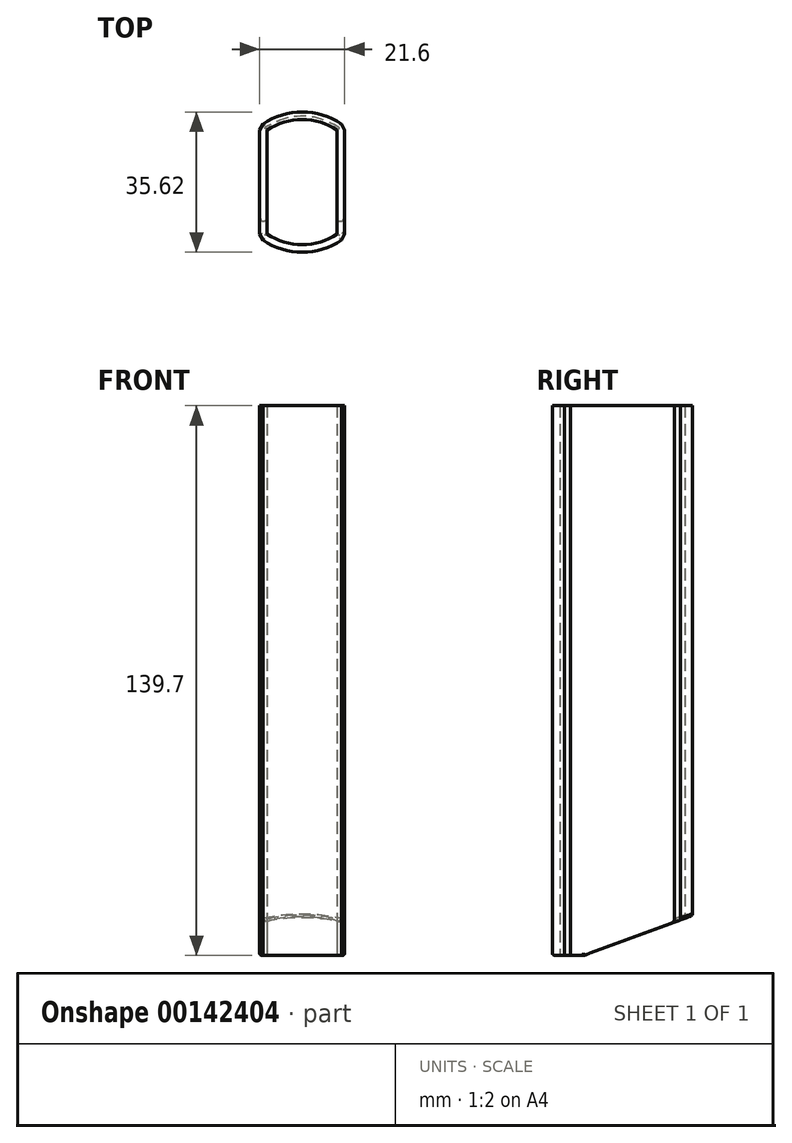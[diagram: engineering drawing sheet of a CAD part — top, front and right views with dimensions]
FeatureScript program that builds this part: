
annotation { "Feature Type Name" : "Feature", "Feature Type Description" : "" }
export const myFeature = defineFeature(function(context is Context, id is Id, definition is map)
    precondition{}
    {
        {
            var Q0;
            Q0=qCreatedBy(makeId("Top.planeOp"),FACE);
            var sketch = newSketch(context, id + "F0", { "sketchPlane" : qUnion([Q0])});
            skLineSegment(sketch, "E0.bottom", {"start": v(-8.9, 13.15) * mm, "end": v(8.9, 13.15) * mm, "construction": true});
            skLineSegment(sketch, "E0.top", {"start": v(-8.9, -13.15) * mm, "end": v(8.9, -13.15) * mm, "construction": true});
            skLineSegment(sketch, "E0.left", {"start": v(-8.9, 13.15) * mm, "end": v(-8.9, -13.15) * mm});
            skLineSegment(sketch, "E0.right", {"start": v(8.9, 13.15) * mm, "end": v(8.9, -13.15) * mm});
            skPoint(sketch, "E0.middle", {"position": v(0, 0) * mm});
            skArc(sketch, "E1", {"start": v(8.9, 13.15) * mm, "mid": v(0, 15.9) * mm, "end": v(-8.9, 13.15) * mm});
            skArc(sketch, "E2", {"start": v(-8.9, -13.15) * mm, "mid": v(0, -15.9) * mm, "end": v(8.89, -13.15) * mm});
            skLineSegment(sketch, "E3.0", {"start": v(-10.8, 13.15) * mm, "end": v(-10.8, -13.15) * mm});
            skArc(sketch, "E4.0", {"start": v(9.97, 14.72) * mm, "mid": v(0, 17.8) * mm, "end": v(-9.97, 14.72) * mm});
            skLineSegment(sketch, "E5.0", {"start": v(10.8, 13.15) * mm, "end": v(10.8, -13.15) * mm});
            skArc(sketch, "E6.0", {"start": v(-9.97, -14.72) * mm, "mid": v(0, -17.8) * mm, "end": v(9.97, -14.72) * mm});
            skLineSegment(sketch, "E7", {"start": v(-10.8, 13.15) * mm, "end": v(-9.97, 14.72) * mm});
            skLineSegment(sketch, "E8", {"start": v(9.97, 14.72) * mm, "end": v(10.8, 13.15) * mm});
            skLineSegment(sketch, "E9", {"start": v(-9.97, -14.72) * mm, "end": v(-10.8, -13.15) * mm});
            skLineSegment(sketch, "E10", {"start": v(9.97, -14.72) * mm, "end": v(10.8, -13.15) * mm});
            skSolve(sketch);
        }
        {
            var Q0;
            Q0=makeQuery(id+"F0.imprint","IMPRINT",FACE,{"disambiguationData":[TD([[makeQuery(id+"F0.imprint","IMPRINT",EDGE,{"derivedFrom":sQuery(id+"F0.wireOp",EDGE,"E0.left")}),-1.0]])]});
            extrude(context, id + "F1", {"entities" : qUnion([Q0]), "depth" : 139.7 * mm});
        }
        {
            var Q0;
            Q0=qCreatedBy(makeId("Right.planeOp"),FACE);
            var sketch = newSketch(context, id + "F2", { "sketchPlane" : qUnion([Q0])});
            skLineSegment(sketch, "E11", {"start": v(-9.84, 0) * mm, "end": v(0, 0) * mm});
            skLineSegment(sketch, "E12", {"start": v(0, 0) * mm, "end": v(24.65, 0) * mm});
            skLineSegment(sketch, "E13", {"start": v(24.65, 0) * mm, "end": v(24.65, 12.7) * mm});
            skLineSegment(sketch, "E14", {"start": v(24.65, 12.7) * mm, "end": v(-9.84, 0) * mm});
            skSolve(sketch);
        }
        {
            var Q0;
            Q0 = qSketchRegion(id + "F2", true);
            extrude(context, id + "F3", {"entities" : qUnion([Q0]), "operationType" : NewBodyOperationType.REMOVE, "endBound" : BoundingType.SYMMETRIC, "oppositeDirection" : true, "depth" : 21.59 * mm});
        }
        {
            var Q0;
            Q0=makeQuery(id+"F3.boolean.opBoolean","COPY",EDGE,{"derivedFrom":makeQuery(id+"F3.opExtrude","CAP_EDGE",EDGE,{"disambiguationData":[OSD([sQuery(id+"F2.wireOp",EDGE,"E14")])],"isStart":false})});
            var Q1;
            Q1=makeQuery(id+"F3.boolean.opBoolean","INTERSECT",EDGE,{"derivedFrom":[makeQuery(id+"F1.opExtrude","SWEPT_FACE",FACE,{"disambiguationData":[OSD([sQuery(id+"F0.wireOp",EDGE,"E4.0")])]}),makeQuery(id+"F3.opExtrude","SWEPT_FACE",FACE,{"disambiguationData":[OSD([sQuery(id+"F2.wireOp",EDGE,"E14")])]})]});
            var Q2;
            Q2=makeQuery(id+"F3.boolean.opBoolean","INTERSECT",EDGE,{"derivedFrom":[makeQuery(id+"F1.opExtrude","SWEPT_FACE",FACE,{"disambiguationData":[OSD([sQuery(id+"F0.wireOp",EDGE,"E1")])]}),makeQuery(id+"F3.opExtrude","SWEPT_FACE",FACE,{"disambiguationData":[OSD([sQuery(id+"F2.wireOp",EDGE,"E14")])]})]});
            var Q3;
            Q3=makeQuery(id+"F3.boolean.opBoolean","INTERSECT",EDGE,{"derivedFrom":[makeQuery(id+"F1.opExtrude","SWEPT_FACE",FACE,{"disambiguationData":[OSD([sQuery(id+"F0.wireOp",EDGE,"E0.right")])]}),makeQuery(id+"F3.opExtrude","SWEPT_FACE",FACE,{"disambiguationData":[OSD([sQuery(id+"F2.wireOp",EDGE,"E14")])]})]});
            var Q4;
            Q4=makeQuery(id+"F3.boolean.opBoolean","COPY",EDGE,{"derivedFrom":makeQuery(id+"F3.opExtrude","CAP_EDGE",EDGE,{"disambiguationData":[OSD([sQuery(id+"F2.wireOp",EDGE,"E14")])],"isStart":true})});
            var Q5;
            Q5=makeQuery(id+"F3.boolean.opBoolean","INTERSECT",EDGE,{"derivedFrom":[makeQuery(id+"F1.opExtrude","SWEPT_FACE",FACE,{"disambiguationData":[OSD([sQuery(id+"F0.wireOp",EDGE,"E8")])]}),makeQuery(id+"F3.opExtrude","SWEPT_FACE",FACE,{"disambiguationData":[OSD([sQuery(id+"F2.wireOp",EDGE,"E14")])]})]});
            var Q6;
            Q6=makeQuery(id+"F3.boolean.opBoolean","INTERSECT",EDGE,{"derivedFrom":[makeQuery(id+"F1.opExtrude","SWEPT_FACE",FACE,{"disambiguationData":[OSD([sQuery(id+"F0.wireOp",EDGE,"E7")])]}),makeQuery(id+"F3.opExtrude","SWEPT_FACE",FACE,{"disambiguationData":[OSD([sQuery(id+"F2.wireOp",EDGE,"E14")])]})]});
            var Q7;
            Q7=makeQuery(id+"F1.opExtrude","CAP_EDGE",EDGE,{"disambiguationData":[OSD([sQuery(id+"F0.wireOp",EDGE,"E3.0")])],"isStart":true});
            var Q8;
            Q8=makeQuery(id+"F1.opExtrude","CAP_EDGE",EDGE,{"disambiguationData":[OSD([sQuery(id+"F0.wireOp",EDGE,"E9")])],"isStart":true});
            var Q9;
            Q9=makeQuery(id+"F1.opExtrude","CAP_EDGE",EDGE,{"disambiguationData":[OSD([sQuery(id+"F0.wireOp",EDGE,"E6.0")])],"isStart":true});
            var Q10;
            Q10=makeQuery(id+"F1.opExtrude","CAP_EDGE",EDGE,{"disambiguationData":[OSD([sQuery(id+"F0.wireOp",EDGE,"E2")])],"isStart":true});
            var Q11;
            Q11=makeQuery(id+"F1.opExtrude","CAP_EDGE",EDGE,{"disambiguationData":[OSD([sQuery(id+"F0.wireOp",EDGE,"E0.right")])],"isStart":true});
            var Q12;
            Q12=makeQuery(id+"F1.opExtrude","CAP_EDGE",EDGE,{"disambiguationData":[OSD([sQuery(id+"F0.wireOp",EDGE,"E5.0")])],"isStart":true});
            var Q13;
            Q13=makeQuery(id+"F1.opExtrude","CAP_EDGE",EDGE,{"disambiguationData":[OSD([sQuery(id+"F0.wireOp",EDGE,"E10")])],"isStart":true});
            var Q14;
            Q14=makeQuery(id+"F1.opExtrude","CAP_EDGE",EDGE,{"disambiguationData":[OSD([sQuery(id+"F0.wireOp",EDGE,"E0.left")])],"isStart":true});
            var Q15;
            Q15=makeQuery(id+"F3.boolean.opBoolean","INTERSECT",EDGE,{"derivedFrom":[makeQuery(id+"F1.opExtrude","SWEPT_FACE",FACE,{"disambiguationData":[OSD([sQuery(id+"F0.wireOp",EDGE,"E0.left")])]}),makeQuery(id+"F3.opExtrude","SWEPT_FACE",FACE,{"disambiguationData":[OSD([sQuery(id+"F2.wireOp",EDGE,"E14")])]})]});
            fillet(context, id + "F4", {"entities" : qUnion([Q0, Q1, Q2, Q3, Q4, Q5, Q6, Q7, Q8, Q9, Q10, Q11, Q12, Q13, Q14, Q15]), "radius" : 0.64 * mm, "tangentPropagation" : true, "allowEdgeOverflow" : false});
        }
    });
